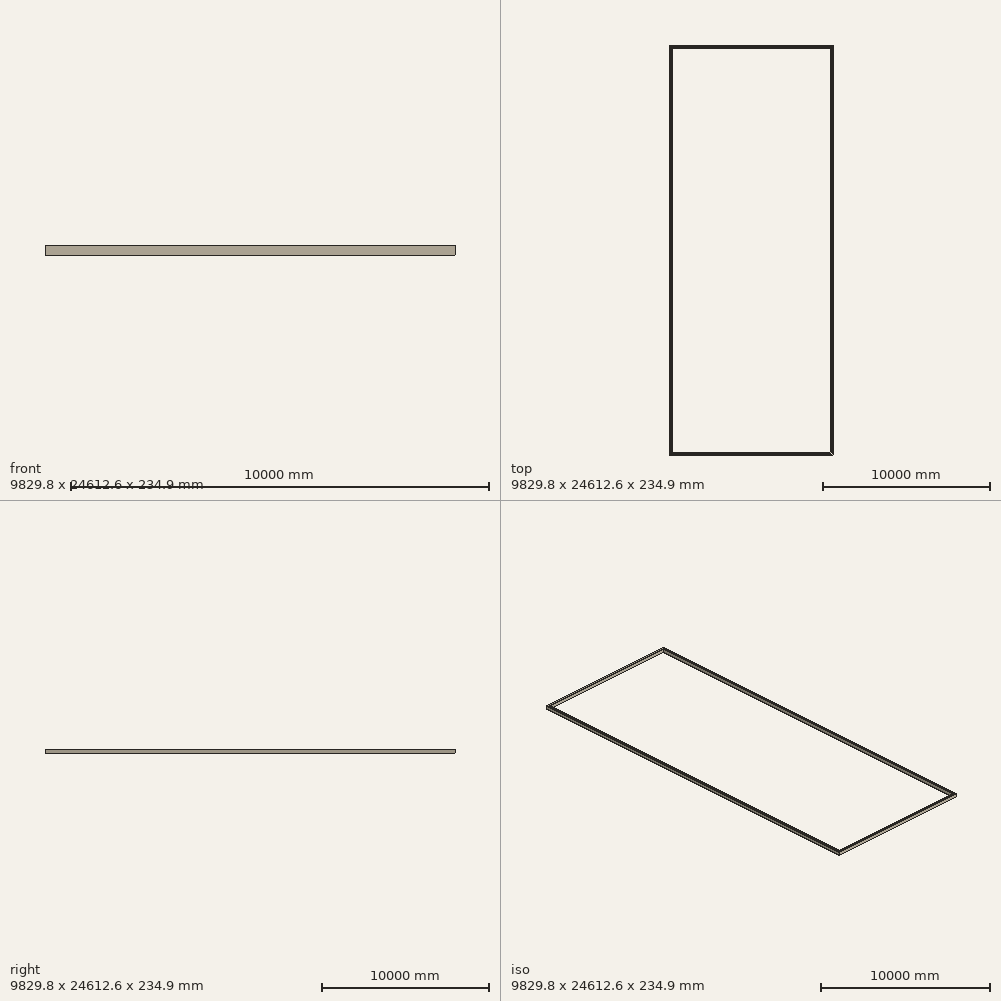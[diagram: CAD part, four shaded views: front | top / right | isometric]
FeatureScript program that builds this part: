
annotation { "Feature Type Name" : "Feature", "Feature Type Description" : "" }
export const myFeature = defineFeature(function(context is Context, id is Id, definition is map)
    precondition{}
    {
        {
            var Q0;
            Q0=qCreatedBy(makeId("Top.planeOp"),FACE);
            var sketch = newSketch(context, id + "F0", { "sketchPlane" : qUnion([Q0])});
            skLineSegment(sketch, "E0.bottom", {"start": v(4876.8, -12268.2) * mm, "end": v(-4876.8, -12268.2) * mm});
            skLineSegment(sketch, "E0.top", {"start": v(4876.8, 12268.2) * mm, "end": v(-4876.8, 12268.2) * mm});
            skLineSegment(sketch, "E0.left", {"start": v(4876.8, -12268.2) * mm, "end": v(4876.8, 12268.2) * mm});
            skLineSegment(sketch, "E0.right", {"start": v(-4876.8, -12268.2) * mm, "end": v(-4876.8, 12268.2) * mm});
            skPoint(sketch, "E0.middle", {"position": v(0, 0) * mm});
            skLineSegment(sketch, "E1.bottom", {"start": v(4914.9, -12306.3) * mm, "end": v(-4914.9, -12306.3) * mm});
            skLineSegment(sketch, "E1.top", {"start": v(4914.9, 12306.3) * mm, "end": v(-4914.9, 12306.3) * mm});
            skLineSegment(sketch, "E1.left", {"start": v(4914.9, -12306.3) * mm, "end": v(4914.9, 12306.3) * mm});
            skLineSegment(sketch, "E1.right", {"start": v(-4914.9, -12306.3) * mm, "end": v(-4914.9, 12306.3) * mm});
            skLineSegment(sketch, "E2.bottom", {"start": v(4787.9, -12179.3) * mm, "end": v(-4787.9, -12179.3) * mm});
            skLineSegment(sketch, "E2.top", {"start": v(4787.9, 12179.3) * mm, "end": v(-4787.9, 12179.3) * mm});
            skLineSegment(sketch, "E2.left", {"start": v(4787.9, -12179.3) * mm, "end": v(4787.9, 12179.3) * mm});
            skLineSegment(sketch, "E2.right", {"start": v(-4787.9, -12179.3) * mm, "end": v(-4787.9, 12179.3) * mm});
            skLineSegment(sketch, "E3.bottom", {"start": v(4749.8, -12141.2) * mm, "end": v(-4749.8, -12141.2) * mm});
            skLineSegment(sketch, "E3.top", {"start": v(4749.8, 12141.2) * mm, "end": v(-4749.8, 12141.2) * mm});
            skLineSegment(sketch, "E3.left", {"start": v(4749.8, -12141.2) * mm, "end": v(4749.8, 12141.2) * mm});
            skLineSegment(sketch, "E3.right", {"start": v(-4749.8, -12141.2) * mm, "end": v(-4749.8, 12141.2) * mm});
            skSolve(sketch);
        }
        {
            var Q0;
            Q0=makeQuery(id+"F0.imprint","IMPRINT",FACE,{"disambiguationData":[TD([[makeQuery(id+"F0.imprint","IMPRINT",EDGE,{"derivedFrom":sQuery(id+"F0.wireOp",EDGE,"E0.bottom")}),1.0]])]});
            var Q1;
            Q1=makeQuery(id+"F0.imprint","IMPRINT",FACE,{"disambiguationData":[TD([[makeQuery(id+"F0.imprint","IMPRINT",EDGE,{"derivedFrom":sQuery(id+"F0.wireOp",EDGE,"E2.bottom")}),-1.0]])]});
            extrude(context, id + "F1", {"entities" : qUnion([Q0, Q1]), "depth" : 234.95 * mm, "offsetDistance" : 30.48 * mm});
        }
    });
